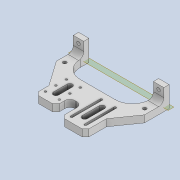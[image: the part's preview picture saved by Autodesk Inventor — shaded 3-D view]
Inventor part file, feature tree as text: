
AUTODESK INVENTOR PART (.ipt)
format: ipt  version: 2020 (Build 240168000, 168)  size: 392,704 bytes
history: native  units: mm
features: reference x10, projected_geometry x10, extrude x9, sketch x9, other x6, thicken_offset x3, fillet x3, plane x1, chamfer x1
ambient origin geometry x8: Origin, YZ Plane, XZ Plane, XY Plane, X Axis, Y Axis, Z Axis, Center Point
bodies: Solid1 (feature_tree)
feature tree (52):
  extrude  "Extrusion1"  Depth=20.0mm
  plane  "Work Plane1"
  extrude  "Extrusion2"  Depth=20.0mm
  extrude  "Extrusion3"  Depth=3.0mm
  extrude  "Extrusion4"  Depth=52.0mm
  thicken_offset  "Thicken1"
  extrude  "Extrusion5"  Depth=4.0mm TaperAngle=0.0deg
  extrude  "Extrusion6"  Depth=24.0mm
  thicken_offset  "Thicken2"
  thicken_offset  "Thicken3"
  fillet  "Fillet1"  Radius=12.0mm
  extrude  "Extrusion7"  Depth=4.0mm TaperAngle=0.0deg
  fillet  "Fillet2"  Radius=12.0mm
  chamfer  "Chamfer1"  Distance=17.0mm
  fillet  "Fillet3"  Radius=1.3mm
  extrude  "Extrusion8"  Depth=17.0mm
  extrude  "Extrusion9"  Depth=3.0mm
  sketch  "Sketch1"  dims[d0=6.0mm d1=20.0mm]
  reference  "Reference1"
  reference  "Reference2"
  sketch  "Sketch2"  dims[d2=6.0mm d3=20.0mm]
  projected_geometry  "Projected Loop1"
  projected_geometry  "Projected Loop2"
  sketch  "Sketch3"  dims[d4=3.0mm d5=0.0mm d6=40.0mm]
  projected_geometry  "Projected Loop3"
  sketch  "Sketch4"  dims[d7=12.0mm d8=52.0mm]
  projected_geometry  "Projected Loop4"
  projected_geometry  "Projected Loop5"
  projected_geometry  "Projected Loop6"
  sketch  "Sketch5"  dims[d9=24.0mm d10=4.0mm d11=0.0mm]
  reference  "Reference3"
  reference  "Reference4"
  reference  "Reference5"
  reference  "Reference6"
  reference  "Reference7"
  reference  "Reference8"
  sketch  "Sketch6"  dims[d12=12.0mm d13=24.0mm d14=12.0mm]
  projected_geometry  "Projected Loop7"
  reference  "Reference9"
  reference  "Reference10"
  sketch  "Sketch7"  dims[d15=24.0mm d16=4.0mm d17=0.0mm d18=12.0mm d19=0.0mm]
  projected_geometry  "Projected Loop8"
  sketch  "Sketch8"  dims[d20=4.0mm]
  projected_geometry  "Projected Loop9"
  sketch  "Sketch9"  dims[d21=4.0mm d22=17.0mm d23=1.3mm d24=17.0mm d25=1.3mm d26=12.0mm d27=0.0mm d28=12.0mm d29=0.0mm d30=1.0mm d31=1.0mm d32=1.0mm d33=1.0mm d34=10.0mm d35=9.599311mm d36=9.599311mm d37=12.0mm d38=0.0mm d39=3.0mm d40=2.0mm d41=2.0mm d42=45.0deg d43=3.0mm d44=4.0mm d45=3.0mm d46=5.0mm d47=3.0mm d48=12.0mm d49=0.0mm d50=5.0mm d51=2.0mm d52=5.0mm d53=2.0mm d54=12.0mm d55=0.0mm]
  projected_geometry  "Projected Loop10"
  parser-record x1  (decoder bookkeeping rows leaked as tree rows — omitted from the tree; the rows remain in map.json)
  other  "tip_3_n_base.iam"
  other  "cpr_shell_1:1"
  other  "bl_tube_ass_2:2"
  other  "bl_tube_hn_1:1"
  other  "bl_tube_ass_2:1"
note: 1 file-system path scrubbed to <path> (originals preserved in map.json)
